# Revit family: FOR UPDATE_26053USA_NEWWWWW
name_source: partatom
category: Plumbing Fixtures
revit_build: Autodesk Revit 2018 (Build: 20170223_1515(x64)
units: mm (PartAtom-declared; Revit-internal decimal feet)

## family parameters
Always vertical = No
Cut with Voids When Loaded = No
OmniClass Number = 23.31.17.00
OmniClass Title = Showers
Part Type = Normal
Room Calculation Point = No
Round Connector Dimension = Use Diameter
Shared = No
Work Plane-Based = Yes

## types (5) — shared parameters
Always visible = Yes
BIMobject category = Showers
Default Elevation = 1219.2 mm  [stored 4 ft]
Description = AXOR ShowerSolutions Hand shower 120 3jet 2.5 GPM
Edition number = 1
IFC Classification = Sanitary Terminal
Manufacturer = AXOR
Manufacturer name = AXOR
Model = 26053USA
OmniClass Code = 23-31 17 00
OmniClass Description = Showers
Product Guid = b4c1eb1f-0c52-4038-95ab-9a51c5eadeea
Product SKU = 26053USA
Product data url = https://bimobject.com
Product family = AXOR ShowerSolutions
Product group = Hand showers
Product name = 26053USA AXOR ShowerSolutions Hand shower 120 3jet 2.5 GPM
Product url = https://www.axor-design.com
QR code = https://bimobject.com
URL = https://www.axor-design.com
Water Inlet = 13 mm
Water Inlet Description = Water Inlet 12.7mm
Weight Net (Kg) = 275

## per-type parameters (varying)
| type | Material 1 |
| 001 Chrome | AXOR - Metal - 001 Chrome |
| 331 Polished Black Chrome | AXOR - Metal - 331 Polished Black Chrome |
| 671 Matt Black | AXOR - Metal - 671 Matt Black |
| 821 Brushed Nickel | AXOR - Metal - 821 Brushed Nickel |
| 991 Polished Gold Optic | AXOR - Metal - 991 Polished Gold Optic |

note: [stored X ft] marks values corroborated as IEEE doubles in the binary element streams (Revit-internal decimal feet)

## geometry (parser evidence)
native form markers: Sweep x2
no freeform markers — native parametric forms only
